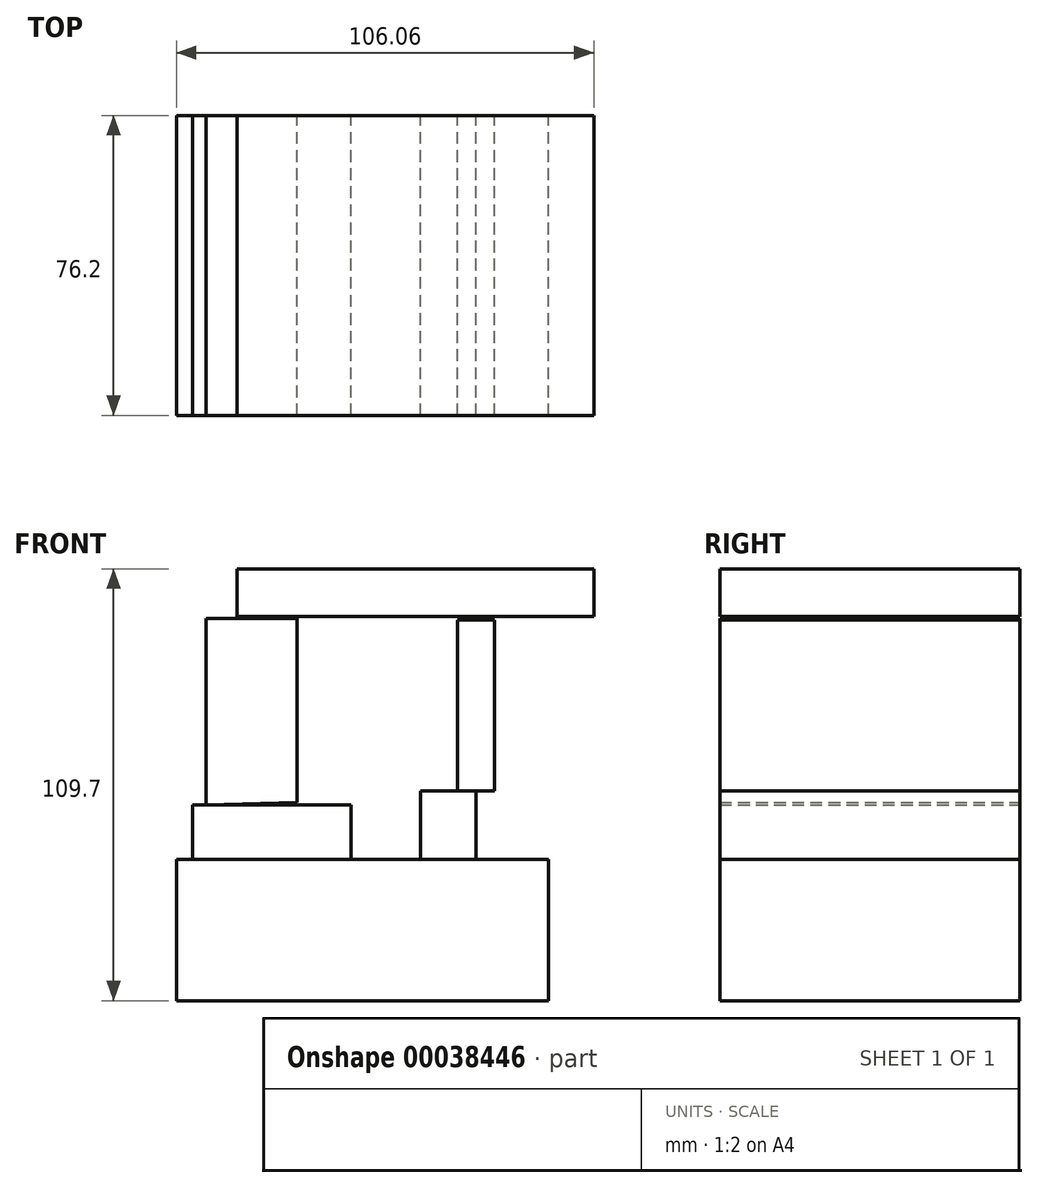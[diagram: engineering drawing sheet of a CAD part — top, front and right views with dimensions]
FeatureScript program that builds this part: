
annotation { "Feature Type Name" : "Feature", "Feature Type Description" : "" }
export const myFeature = defineFeature(function(context is Context, id is Id, definition is map)
    precondition{}
    {
        {
            var Q0;
            Q0=qCreatedBy(makeId("Front.planeOp"),FACE);
            var sketch = newSketch(context, id + "F0", { "sketchPlane" : qUnion([Q0])});
            skLineSegment(sketch, "E0.bottom", {"start": v(-44.31, 0) * mm, "end": v(50.26, 0) * mm});
            skLineSegment(sketch, "E0.top", {"start": v(-44.31, -35.86) * mm, "end": v(50.26, -35.86) * mm});
            skLineSegment(sketch, "E0.left", {"start": v(-44.31, 0) * mm, "end": v(-44.31, -35.86) * mm});
            skLineSegment(sketch, "E0.right", {"start": v(50.26, 0) * mm, "end": v(50.26, -35.86) * mm});
            skSolve(sketch);
        }
        {
            var Q0;
            Q0=makeQuery(id+"F0.imprint","IMPRINT",FACE,{"disambiguationData":[TD([[makeQuery(id+"F0.imprint","IMPRINT",EDGE,{"derivedFrom":sQuery(id+"F0.wireOp",EDGE,"E0.bottom")}),-1.0]])]});
            extrude(context, id + "F1", {"entities" : qUnion([Q0]), "depth" : 76.2 * mm});
        }
        {
            var Q0;
            Q0=qCreatedBy(makeId("Front.planeOp"),FACE);
            var sketch = newSketch(context, id + "F2", { "sketchPlane" : qUnion([Q0])});
            skLineSegment(sketch, "E1", {"start": v(-40.24, 0) * mm, "end": v(-40.24, 13.94) * mm});
            skLineSegment(sketch, "E2", {"start": v(-40.24, 13.94) * mm, "end": v(0, 13.94) * mm});
            skLineSegment(sketch, "E3", {"start": v(0, 13.94) * mm, "end": v(0, 0) * mm});
            skLineSegment(sketch, "E4", {"start": v(0, 0) * mm, "end": v(-40.24, 0) * mm});
            skSolve(sketch);
        }
        {
            var Q0;
            Q0=makeQuery(id+"F2.imprint","IMPRINT",FACE,{"disambiguationData":[TD([[makeQuery(id+"F2.imprint","IMPRINT",EDGE,{"derivedFrom":sQuery(id+"F2.wireOp",EDGE,"E1")}),-1.0]])]});
            extrude(context, id + "F3", {"entities" : qUnion([Q0]), "depth" : 76.2 * mm});
        }
        {
            var Q0;
            Q0=qCreatedBy(makeId("Front.planeOp"),FACE);
            var sketch = newSketch(context, id + "F4", { "sketchPlane" : qUnion([Q0])});
            skLineSegment(sketch, "E5", {"start": v(-36.8, 13.94) * mm, "end": v(-36.8, 61.22) * mm});
            skLineSegment(sketch, "E6", {"start": v(-36.8, 61.22) * mm, "end": v(-13.62, 61.22) * mm});
            skLineSegment(sketch, "E7", {"start": v(-13.62, 61.22) * mm, "end": v(-13.62, 14.56) * mm});
            skLineSegment(sketch, "E8", {"start": v(-13.62, 14.56) * mm, "end": v(-36.8, 13.94) * mm});
            skSolve(sketch);
        }
        {
            var Q0;
            Q0=makeQuery(id+"F4.imprint","IMPRINT",FACE,{"disambiguationData":[TD([[makeQuery(id+"F4.imprint","IMPRINT",EDGE,{"derivedFrom":sQuery(id+"F4.wireOp",EDGE,"E5")}),-1.0]])]});
            extrude(context, id + "F5", {"entities" : qUnion([Q0]), "depth" : 76.2 * mm});
        }
        {
            var Q0;
            Q0=qCreatedBy(makeId("Front.planeOp"),FACE);
            var sketch = newSketch(context, id + "F6", { "sketchPlane" : qUnion([Q0])});
            skLineSegment(sketch, "E9.bottom", {"start": v(-28.96, 73.84) * mm, "end": v(61.75, 73.84) * mm});
            skLineSegment(sketch, "E9.top", {"start": v(-28.96, 61.72) * mm, "end": v(61.75, 61.72) * mm});
            skLineSegment(sketch, "E9.left", {"start": v(-28.96, 73.84) * mm, "end": v(-28.96, 61.72) * mm});
            skLineSegment(sketch, "E9.right", {"start": v(61.75, 73.84) * mm, "end": v(61.75, 61.72) * mm});
            skSolve(sketch);
        }
        {
            var Q0;
            Q0=makeQuery(id+"F6.imprint","IMPRINT",FACE,{"disambiguationData":[TD([[makeQuery(id+"F6.imprint","IMPRINT",EDGE,{"derivedFrom":sQuery(id+"F6.wireOp",EDGE,"E9.bottom")}),-1.0]])]});
            extrude(context, id + "F7", {"entities" : qUnion([Q0]), "depth" : 76.2 * mm});
        }
        {
            var Q0;
            Q0=qCreatedBy(makeId("Front.planeOp"),FACE);
            var sketch = newSketch(context, id + "F8", { "sketchPlane" : qUnion([Q0])});
            skLineSegment(sketch, "E10.bottom", {"start": v(27.09, 60.9) * mm, "end": v(36.48, 60.9) * mm});
            skLineSegment(sketch, "E10.top", {"start": v(27.09, 17.38) * mm, "end": v(36.48, 17.38) * mm});
            skLineSegment(sketch, "E10.left", {"start": v(27.09, 60.9) * mm, "end": v(27.09, 17.38) * mm});
            skLineSegment(sketch, "E10.right", {"start": v(36.48, 60.9) * mm, "end": v(36.48, 17.38) * mm});
            skPoint(sketch, "E11.firstSnap0", {"position": v(31.78, 17.38) * mm});
            skPoint(sketch, "E11.oppositeSnap0", {"position": v(31.78, 17.38) * mm});
            skLineSegment(sketch, "E11.bottom", {"start": v(17.7, 17.38) * mm, "end": v(31.78, 17.38) * mm});
            skLineSegment(sketch, "E11.top", {"start": v(17.7, 0) * mm, "end": v(31.78, 0) * mm});
            skLineSegment(sketch, "E11.left", {"start": v(17.7, 17.38) * mm, "end": v(17.7, 0) * mm});
            skLineSegment(sketch, "E11.right", {"start": v(31.78, 17.38) * mm, "end": v(31.78, 0) * mm});
            skSolve(sketch);
        }
        {
            var Q0;
            Q0=makeQuery(id+"F8.imprint","IMPRINT",FACE,{"disambiguationData":[TD([[makeQuery(id+"F8.imprint","IMPRINT",EDGE,{"derivedFrom":sQuery(id+"F8.wireOp",EDGE,"E10.bottom")}),-1.0]])]});
            extrude(context, id + "F9", {"entities" : qUnion([Q0]), "depth" : 76.2 * mm});
        }
        {
            var Q0;
            Q0 = qSketchRegion(id + "F8", true);
            extrude(context, id + "F10", {"entities" : qUnion([Q0]), "depth" : 76.2 * mm});
        }
    });
